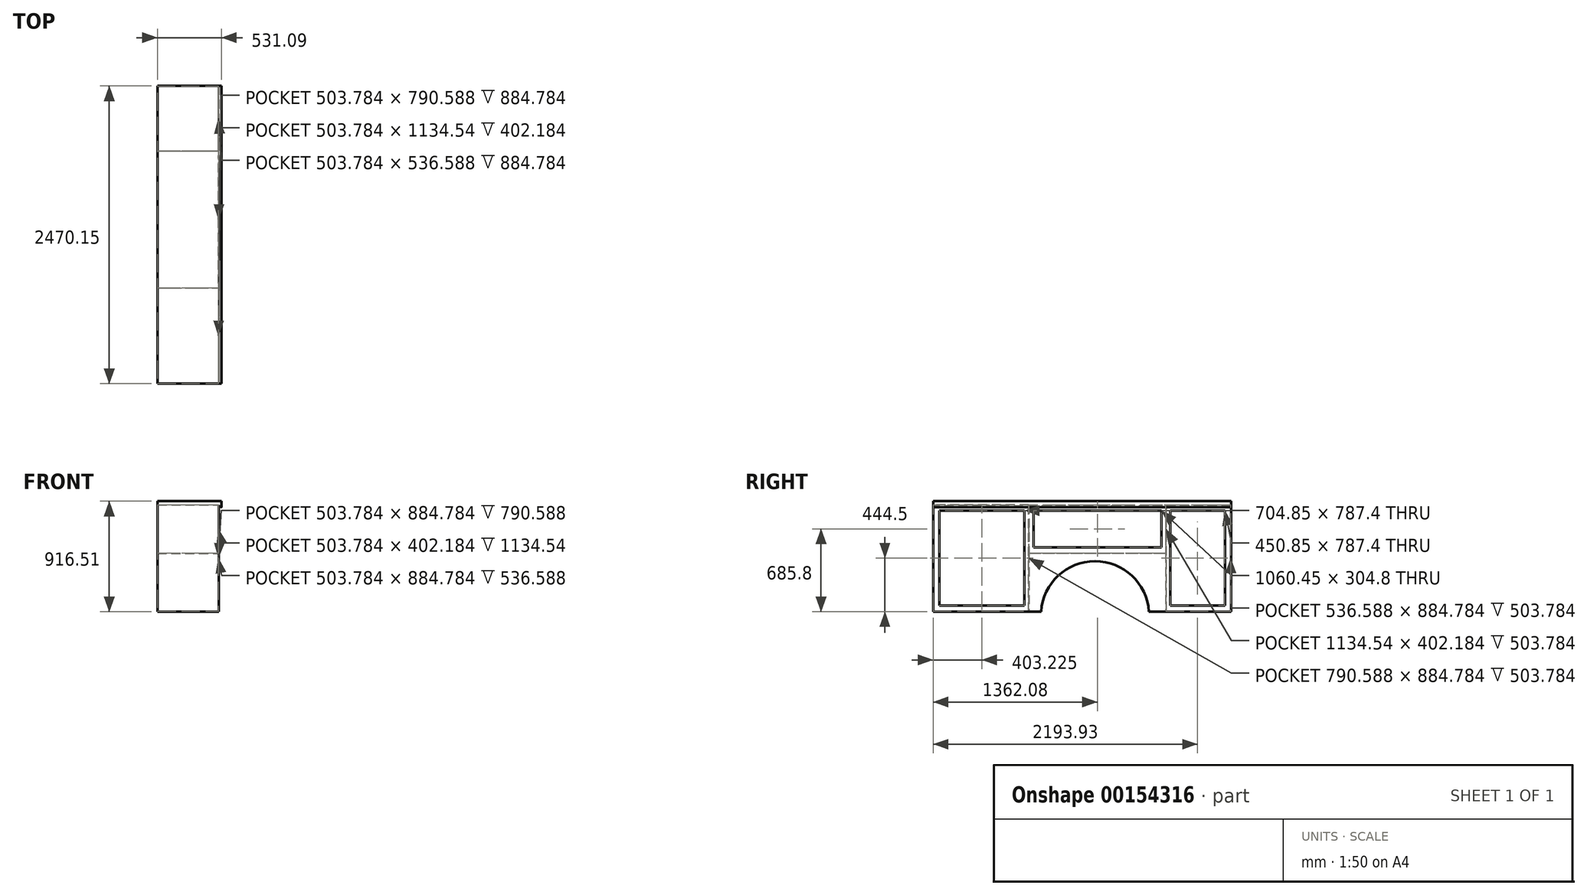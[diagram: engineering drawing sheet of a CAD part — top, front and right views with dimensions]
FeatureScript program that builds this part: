
annotation { "Feature Type Name" : "Feature", "Feature Type Description" : "" }
export const myFeature = defineFeature(function(context is Context, id is Id, definition is map)
    precondition{}
    {
        {
            var Q0;
            Q0=qCreatedBy(makeId("Front.planeOp"),FACE);
            var sketch = newSketch(context, id + "F0", { "sketchPlane" : qUnion([Q0])});
            skLineSegment(sketch, "E0.bottom", {"start": v(-254, 457.2) * mm, "end": v(254, 457.2) * mm});
            skLineSegment(sketch, "E0.top", {"start": v(-254, -457.2) * mm, "end": v(254, -457.2) * mm});
            skLineSegment(sketch, "E0.left", {"start": v(-254, 457.2) * mm, "end": v(-254, -457.2) * mm});
            skLineSegment(sketch, "E0.right", {"start": v(254, 457.2) * mm, "end": v(254, -457.2) * mm});
            skPoint(sketch, "E0.middle", {"position": v(0, 0) * mm});
            skSolve(sketch);
        }
        {
            var Q0;
            Q0 = qSketchRegion(id + "F0", true);
            extrude(context, id + "F1", {"entities" : qUnion([Q0]), "oppositeDirection" : true, "depth" : 2470.15 * mm});
        }
        {
            var Q0;
            Q0=makeQuery(id+"F1.opExtrude","SWEPT_FACE",FACE,{"disambiguationData":[OSD([sQuery(id+"F0.wireOp",EDGE,"E0.right")])]});
            var sketch = newSketch(context, id + "F2", { "sketchPlane" : qUnion([Q0])});
            skLineSegment(sketch, "E1", {"start": v(793.75, 457.2) * mm, "end": v(793.75, -457.2) * mm});
            skLineSegment(sketch, "E2", {"start": v(1930.4, 457.2) * mm, "end": v(1930.4, -457.2) * mm});
            skLineSegment(sketch, "E3", {"start": v(793.75, 25.4) * mm, "end": v(1930.4, 25.4) * mm});
            skLineSegment(sketch, "E4.bottom", {"start": v(755.65, -406.4) * mm, "end": v(50.8, -406.4) * mm});
            skLineSegment(sketch, "E4.top", {"start": v(755.65, 381) * mm, "end": v(50.8, 381) * mm});
            skLineSegment(sketch, "E4.left", {"start": v(755.65, -406.4) * mm, "end": v(755.65, 381) * mm});
            skLineSegment(sketch, "E4.right", {"start": v(50.8, -406.4) * mm, "end": v(50.8, 381) * mm});
            skLineSegment(sketch, "E5.bottom", {"start": v(831.85, 381) * mm, "end": v(1892.3, 381) * mm});
            skLineSegment(sketch, "E5.top", {"start": v(831.85, 76.2) * mm, "end": v(1892.3, 76.2) * mm});
            skLineSegment(sketch, "E5.left", {"start": v(831.85, 381) * mm, "end": v(831.85, 76.2) * mm});
            skLineSegment(sketch, "E5.right", {"start": v(1892.3, 381) * mm, "end": v(1892.3, 76.2) * mm});
            skLineSegment(sketch, "E6.bottom", {"start": v(1968.5, 381) * mm, "end": v(2419.35, 381) * mm});
            skLineSegment(sketch, "E6.top", {"start": v(1968.5, -406.4) * mm, "end": v(2419.35, -406.4) * mm});
            skLineSegment(sketch, "E6.left", {"start": v(1968.5, 381) * mm, "end": v(1968.5, -406.4) * mm});
            skLineSegment(sketch, "E6.right", {"start": v(2419.35, 381) * mm, "end": v(2419.35, -406.4) * mm});
            skSolve(sketch);
        }
        {
            var Q0;
            Q0 = qSketchRegion(id + "F2", true);
            extrude(context, id + "F3", {"entities" : qUnion([Q0]), "operationType" : NewBodyOperationType.REMOVE, "oppositeDirection" : true, "depth" : 505.9 * mm});
        }
        {
            var Q0;
            Q0=makeQuery(id+"F3.boolean.opBoolean","COPY",FACE,{"derivedFrom":makeQuery(id+"F3.opExtrude","SWEPT_FACE",FACE,{"disambiguationData":[OSD([sQuery(id+"F2.wireOp",EDGE,"E4.bottom")])]})});
            var sketch = newSketch(context, id + "F4", { "sketchPlane" : qUnion([Q0])});
            skLineSegment(sketch, "E7.bottom", {"start": v(-251.9, 755.65) * mm, "end": v(251.9, 755.65) * mm});
            skLineSegment(sketch, "E7.top", {"start": v(-251.9, 50.8) * mm, "end": v(251.9, 50.8) * mm});
            skLineSegment(sketch, "E7.left", {"start": v(-251.9, 755.65) * mm, "end": v(-251.9, 50.8) * mm});
            skLineSegment(sketch, "E7.right", {"start": v(251.9, 755.65) * mm, "end": v(251.9, 50.8) * mm});
            skSolve(sketch);
        }
        {
            var Q0;
            Q0 = qSketchRegion(id + "F4", true);
            extrude(context, id + "F5", {"entities" : qUnion([Q0]), "operationType" : NewBodyOperationType.REMOVE, "oppositeDirection" : true, "depth" : 48.7 * mm});
        }
        {
            var Q0;
            Q0=makeQuery(id+"F3.boolean.opBoolean","COPY",FACE,{"derivedFrom":makeQuery(id+"F3.opExtrude","SWEPT_FACE",FACE,{"disambiguationData":[OSD([sQuery(id+"F2.wireOp",EDGE,"E4.top")])]})});
            var sketch = newSketch(context, id + "F6", { "sketchPlane" : qUnion([Q0])});
            skLineSegment(sketch, "E8.bottom", {"start": v(-251.9, -755.65) * mm, "end": v(251.9, -755.65) * mm});
            skLineSegment(sketch, "E8.top", {"start": v(-251.9, -50.8) * mm, "end": v(251.9, -50.8) * mm});
            skLineSegment(sketch, "E8.left", {"start": v(-251.9, -755.65) * mm, "end": v(-251.9, -50.8) * mm});
            skLineSegment(sketch, "E8.right", {"start": v(251.9, -755.65) * mm, "end": v(251.9, -50.8) * mm});
            skSolve(sketch);
        }
        {
            var Q0;
            Q0 = qSketchRegion(id + "F6", true);
            extrude(context, id + "F7", {"entities" : qUnion([Q0]), "operationType" : NewBodyOperationType.REMOVE, "oppositeDirection" : true, "depth" : 48.7 * mm});
        }
        {
            var Q0;
            Q0=makeQuery(id+"F7.boolean.opBoolean","MERGE",FACE,{"derivedFrom":[makeQuery(id+"F5.boolean.opBoolean","MERGE",FACE,{"derivedFrom":[makeQuery(id+"F3.boolean.opBoolean","COPY",FACE,{"derivedFrom":makeQuery(id+"F3.opExtrude","SWEPT_FACE",FACE,{"disambiguationData":[OSD([sQuery(id+"F2.wireOp",EDGE,"E4.right")])]})}),makeQuery(id+"F5.opExtrude","SWEPT_FACE",FACE,{"disambiguationData":[OSD([sQuery(id+"F4.wireOp",EDGE,"E7.top")])]})]}),makeQuery(id+"F7.opExtrude","SWEPT_FACE",FACE,{"disambiguationData":[OSD([sQuery(id+"F6.wireOp",EDGE,"E8.top")])]})]});
            var sketch = newSketch(context, id + "F8", { "sketchPlane" : qUnion([Q0])});
            skLineSegment(sketch, "E9.bottom", {"start": v(251.9, 429.7) * mm, "end": v(-251.9, 429.7) * mm});
            skLineSegment(sketch, "E9.top", {"start": v(251.9, -455.1) * mm, "end": v(-251.9, -455.1) * mm});
            skLineSegment(sketch, "E9.left", {"start": v(251.9, 429.7) * mm, "end": v(251.9, -455.1) * mm});
            skLineSegment(sketch, "E9.right", {"start": v(-251.9, 429.7) * mm, "end": v(-251.9, -455.1) * mm});
            skSolve(sketch);
        }
        {
            var Q0;
            Q0 = qSketchRegion(id + "F8", true);
            extrude(context, id + "F9", {"entities" : qUnion([Q0]), "operationType" : NewBodyOperationType.REMOVE, "oppositeDirection" : true, "depth" : 48.7 * mm});
        }
        {
            var Q0;
            Q0=makeQuery(id+"F7.boolean.opBoolean","MERGE",FACE,{"derivedFrom":[makeQuery(id+"F5.boolean.opBoolean","MERGE",FACE,{"derivedFrom":[makeQuery(id+"F3.boolean.opBoolean","COPY",FACE,{"derivedFrom":makeQuery(id+"F3.opExtrude","SWEPT_FACE",FACE,{"disambiguationData":[OSD([sQuery(id+"F2.wireOp",EDGE,"E4.left")])]})}),makeQuery(id+"F5.opExtrude","SWEPT_FACE",FACE,{"disambiguationData":[OSD([sQuery(id+"F4.wireOp",EDGE,"E7.bottom")])]})]}),makeQuery(id+"F7.opExtrude","SWEPT_FACE",FACE,{"disambiguationData":[OSD([sQuery(id+"F6.wireOp",EDGE,"E8.bottom")])]})]});
            var sketch = newSketch(context, id + "F10", { "sketchPlane" : qUnion([Q0])});
            skLineSegment(sketch, "E10.bottom", {"start": v(-251.9, -455.1) * mm, "end": v(251.9, -455.1) * mm});
            skLineSegment(sketch, "E10.top", {"start": v(-251.9, 429.7) * mm, "end": v(251.9, 429.7) * mm});
            skLineSegment(sketch, "E10.left", {"start": v(-251.9, -455.1) * mm, "end": v(-251.9, 429.7) * mm});
            skLineSegment(sketch, "E10.right", {"start": v(251.9, -455.1) * mm, "end": v(251.9, 429.7) * mm});
            skSolve(sketch);
        }
        {
            var Q0;
            Q0 = qSketchRegion(id + "F10", true);
            extrude(context, id + "F11", {"entities" : qUnion([Q0]), "operationType" : NewBodyOperationType.REMOVE, "oppositeDirection" : true, "depth" : 37.05 * mm});
        }
        {
            var Q0;
            Q0=makeQuery(id+"F3.boolean.opBoolean","COPY",FACE,{"derivedFrom":makeQuery(id+"F3.opExtrude","SWEPT_FACE",FACE,{"disambiguationData":[OSD([sQuery(id+"F2.wireOp",EDGE,"E5.top")])]})});
            var sketch = newSketch(context, id + "F12", { "sketchPlane" : qUnion([Q0])});
            skLineSegment(sketch, "E11.bottom", {"start": v(-251.9, 831.85) * mm, "end": v(251.9, 831.85) * mm});
            skLineSegment(sketch, "E11.top", {"start": v(-251.9, 1892.3) * mm, "end": v(251.9, 1892.3) * mm});
            skLineSegment(sketch, "E11.left", {"start": v(-251.9, 831.85) * mm, "end": v(-251.9, 1892.3) * mm});
            skLineSegment(sketch, "E11.right", {"start": v(251.9, 831.85) * mm, "end": v(251.9, 1892.3) * mm});
            skSolve(sketch);
        }
        {
            var Q0;
            Q0 = qSketchRegion(id + "F12", true);
            extrude(context, id + "F13", {"entities" : qUnion([Q0]), "operationType" : NewBodyOperationType.REMOVE, "oppositeDirection" : true, "depth" : 48.7 * mm});
        }
        {
            var Q0;
            Q0=makeQuery(id+"F3.boolean.opBoolean","COPY",FACE,{"derivedFrom":makeQuery(id+"F3.opExtrude","SWEPT_FACE",FACE,{"disambiguationData":[OSD([sQuery(id+"F2.wireOp",EDGE,"E5.bottom")])]})});
            var sketch = newSketch(context, id + "F14", { "sketchPlane" : qUnion([Q0])});
            skLineSegment(sketch, "E12.bottom", {"start": v(-251.9, -1892.3) * mm, "end": v(251.9, -1892.3) * mm});
            skLineSegment(sketch, "E12.top", {"start": v(-251.9, -831.85) * mm, "end": v(251.9, -831.85) * mm});
            skLineSegment(sketch, "E12.left", {"start": v(-251.9, -1892.3) * mm, "end": v(-251.9, -831.85) * mm});
            skLineSegment(sketch, "E12.right", {"start": v(251.9, -1892.3) * mm, "end": v(251.9, -831.85) * mm});
            skSolve(sketch);
        }
        {
            var Q0;
            Q0 = qSketchRegion(id + "F14", true);
            extrude(context, id + "F15", {"entities" : qUnion([Q0]), "operationType" : NewBodyOperationType.REMOVE, "oppositeDirection" : true, "depth" : 48.7 * mm});
        }
        {
            var Q0;
            Q0=makeQuery(id+"F15.boolean.opBoolean","MERGE",FACE,{"derivedFrom":[makeQuery(id+"F13.boolean.opBoolean","MERGE",FACE,{"derivedFrom":[makeQuery(id+"F3.boolean.opBoolean","COPY",FACE,{"derivedFrom":makeQuery(id+"F3.opExtrude","SWEPT_FACE",FACE,{"disambiguationData":[OSD([sQuery(id+"F2.wireOp",EDGE,"E5.left")])]})}),makeQuery(id+"F13.opExtrude","SWEPT_FACE",FACE,{"disambiguationData":[OSD([sQuery(id+"F12.wireOp",EDGE,"E11.bottom")])]})]}),makeQuery(id+"F15.opExtrude","SWEPT_FACE",FACE,{"disambiguationData":[OSD([sQuery(id+"F14.wireOp",EDGE,"E12.top")])]})]});
            var sketch = newSketch(context, id + "F16", { "sketchPlane" : qUnion([Q0])});
            skLineSegment(sketch, "E13.bottom", {"start": v(251.9, 429.7) * mm, "end": v(-251.9, 429.7) * mm});
            skLineSegment(sketch, "E13.top", {"start": v(251.9, 27.5) * mm, "end": v(-251.9, 27.5) * mm});
            skLineSegment(sketch, "E13.left", {"start": v(251.9, 429.7) * mm, "end": v(251.9, 27.5) * mm});
            skLineSegment(sketch, "E13.right", {"start": v(-251.9, 429.7) * mm, "end": v(-251.9, 27.5) * mm});
            skSolve(sketch);
        }
        {
            var Q0;
            Q0 = qSketchRegion(id + "F16", true);
            extrude(context, id + "F17", {"entities" : qUnion([Q0]), "operationType" : NewBodyOperationType.REMOVE, "oppositeDirection" : true, "depth" : 37.05 * mm});
        }
        {
            var Q0;
            Q0=makeQuery(id+"F15.boolean.opBoolean","MERGE",FACE,{"derivedFrom":[makeQuery(id+"F13.boolean.opBoolean","MERGE",FACE,{"derivedFrom":[makeQuery(id+"F3.boolean.opBoolean","COPY",FACE,{"derivedFrom":makeQuery(id+"F3.opExtrude","SWEPT_FACE",FACE,{"disambiguationData":[OSD([sQuery(id+"F2.wireOp",EDGE,"E5.right")])]})}),makeQuery(id+"F13.opExtrude","SWEPT_FACE",FACE,{"disambiguationData":[OSD([sQuery(id+"F12.wireOp",EDGE,"E11.top")])]})]}),makeQuery(id+"F15.opExtrude","SWEPT_FACE",FACE,{"disambiguationData":[OSD([sQuery(id+"F14.wireOp",EDGE,"E12.bottom")])]})]});
            var sketch = newSketch(context, id + "F18", { "sketchPlane" : qUnion([Q0])});
            skLineSegment(sketch, "E14.bottom", {"start": v(-251.9, 429.7) * mm, "end": v(251.9, 429.7) * mm});
            skLineSegment(sketch, "E14.top", {"start": v(-251.9, 27.5) * mm, "end": v(251.9, 27.5) * mm});
            skLineSegment(sketch, "E14.left", {"start": v(-251.9, 429.7) * mm, "end": v(-251.9, 27.5) * mm});
            skLineSegment(sketch, "E14.right", {"start": v(251.9, 429.7) * mm, "end": v(251.9, 27.5) * mm});
            skSolve(sketch);
        }
        {
            var Q0;
            Q0 = qSketchRegion(id + "F18", true);
            extrude(context, id + "F19", {"entities" : qUnion([Q0]), "operationType" : NewBodyOperationType.REMOVE, "oppositeDirection" : true, "depth" : 37.05 * mm});
        }
        {
            var Q0;
            Q0=makeQuery(id+"F3.boolean.opBoolean","COPY",FACE,{"derivedFrom":makeQuery(id+"F3.opExtrude","SWEPT_FACE",FACE,{"disambiguationData":[OSD([sQuery(id+"F2.wireOp",EDGE,"E6.top")])]})});
            var sketch = newSketch(context, id + "F20", { "sketchPlane" : qUnion([Q0])});
            skLineSegment(sketch, "E15.bottom", {"start": v(-251.9, 1968.5) * mm, "end": v(251.9, 1968.5) * mm});
            skLineSegment(sketch, "E15.top", {"start": v(-251.9, 2419.35) * mm, "end": v(251.9, 2419.35) * mm});
            skLineSegment(sketch, "E15.left", {"start": v(-251.9, 1968.5) * mm, "end": v(-251.9, 2419.35) * mm});
            skLineSegment(sketch, "E15.right", {"start": v(251.9, 1968.5) * mm, "end": v(251.9, 2419.35) * mm});
            skSolve(sketch);
        }
        {
            var Q0;
            Q0 = qSketchRegion(id + "F20", true);
            extrude(context, id + "F21", {"entities" : qUnion([Q0]), "operationType" : NewBodyOperationType.REMOVE, "oppositeDirection" : true, "depth" : 48.7 * mm});
        }
        {
            var Q0;
            Q0=makeQuery(id+"F3.boolean.opBoolean","COPY",FACE,{"derivedFrom":makeQuery(id+"F3.opExtrude","SWEPT_FACE",FACE,{"disambiguationData":[OSD([sQuery(id+"F2.wireOp",EDGE,"E6.bottom")])]})});
            var sketch = newSketch(context, id + "F22", { "sketchPlane" : qUnion([Q0])});
            skLineSegment(sketch, "E16.bottom", {"start": v(-251.9, -1968.5) * mm, "end": v(251.9, -1968.5) * mm});
            skLineSegment(sketch, "E16.top", {"start": v(-251.9, -2419.35) * mm, "end": v(251.9, -2419.35) * mm});
            skLineSegment(sketch, "E16.left", {"start": v(-251.9, -1968.5) * mm, "end": v(-251.9, -2419.35) * mm});
            skLineSegment(sketch, "E16.right", {"start": v(251.9, -1968.5) * mm, "end": v(251.9, -2419.35) * mm});
            skSolve(sketch);
        }
        {
            var Q0;
            Q0 = qSketchRegion(id + "F22", true);
            extrude(context, id + "F23", {"entities" : qUnion([Q0]), "operationType" : NewBodyOperationType.REMOVE, "oppositeDirection" : true, "depth" : 48.7 * mm});
        }
        {
            var Q0;
            Q0=makeQuery(id+"F23.boolean.opBoolean","MERGE",FACE,{"derivedFrom":[makeQuery(id+"F21.boolean.opBoolean","MERGE",FACE,{"derivedFrom":[makeQuery(id+"F3.boolean.opBoolean","COPY",FACE,{"derivedFrom":makeQuery(id+"F3.opExtrude","SWEPT_FACE",FACE,{"disambiguationData":[OSD([sQuery(id+"F2.wireOp",EDGE,"E6.left")])]})}),makeQuery(id+"F21.opExtrude","SWEPT_FACE",FACE,{"disambiguationData":[OSD([sQuery(id+"F20.wireOp",EDGE,"E15.bottom")])]})]}),makeQuery(id+"F23.opExtrude","SWEPT_FACE",FACE,{"disambiguationData":[OSD([sQuery(id+"F22.wireOp",EDGE,"E16.bottom")])]})]});
            var sketch = newSketch(context, id + "F24", { "sketchPlane" : qUnion([Q0])});
            skLineSegment(sketch, "E17.bottom", {"start": v(251.9, -455.1) * mm, "end": v(-251.9, -455.1) * mm});
            skLineSegment(sketch, "E17.top", {"start": v(251.9, 429.7) * mm, "end": v(-251.9, 429.7) * mm});
            skLineSegment(sketch, "E17.left", {"start": v(251.9, -455.1) * mm, "end": v(251.9, 429.7) * mm});
            skLineSegment(sketch, "E17.right", {"start": v(-251.9, -455.1) * mm, "end": v(-251.9, 429.7) * mm});
            skSolve(sketch);
        }
        {
            var Q0;
            Q0 = qSketchRegion(id + "F24", true);
            extrude(context, id + "F25", {"entities" : qUnion([Q0]), "operationType" : NewBodyOperationType.REMOVE, "oppositeDirection" : true, "depth" : 37.05 * mm});
        }
        {
            var Q0;
            Q0=makeQuery(id+"F23.boolean.opBoolean","MERGE",FACE,{"derivedFrom":[makeQuery(id+"F21.boolean.opBoolean","MERGE",FACE,{"derivedFrom":[makeQuery(id+"F3.boolean.opBoolean","COPY",FACE,{"derivedFrom":makeQuery(id+"F3.opExtrude","SWEPT_FACE",FACE,{"disambiguationData":[OSD([sQuery(id+"F2.wireOp",EDGE,"E6.right")])]})}),makeQuery(id+"F21.opExtrude","SWEPT_FACE",FACE,{"disambiguationData":[OSD([sQuery(id+"F20.wireOp",EDGE,"E15.top")])]})]}),makeQuery(id+"F23.opExtrude","SWEPT_FACE",FACE,{"disambiguationData":[OSD([sQuery(id+"F22.wireOp",EDGE,"E16.top")])]})]});
            var sketch = newSketch(context, id + "F26", { "sketchPlane" : qUnion([Q0])});
            skLineSegment(sketch, "E18.bottom", {"start": v(-251.9, -455.1) * mm, "end": v(251.9, -455.1) * mm});
            skLineSegment(sketch, "E18.top", {"start": v(-251.9, 429.7) * mm, "end": v(251.9, 429.7) * mm});
            skLineSegment(sketch, "E18.left", {"start": v(-251.9, -455.1) * mm, "end": v(-251.9, 429.7) * mm});
            skLineSegment(sketch, "E18.right", {"start": v(251.9, -455.1) * mm, "end": v(251.9, 429.7) * mm});
            skSolve(sketch);
        }
        {
            var Q0;
            Q0 = qSketchRegion(id + "F26", true);
            extrude(context, id + "F27", {"entities" : qUnion([Q0]), "operationType" : NewBodyOperationType.REMOVE, "oppositeDirection" : true, "depth" : 48.7 * mm});
        }
        {
            var Q0;
            Q0=makeQuery(id+"F1.opExtrude","SWEPT_FACE",FACE,{"disambiguationData":[OSD([sQuery(id+"F0.wireOp",EDGE,"E0.top")])]});
            var sketch = newSketch(context, id + "F28", { "sketchPlane" : qUnion([Q0])});
            skLineSegment(sketch, "E19.bottom", {"start": v(-254, -1929.35) * mm, "end": v(251.9, -1929.35) * mm});
            skLineSegment(sketch, "E19.top", {"start": v(-254, -794.8) * mm, "end": v(251.9, -794.8) * mm});
            skLineSegment(sketch, "E19.left", {"start": v(-254, -1929.35) * mm, "end": v(-254, -794.8) * mm});
            skLineSegment(sketch, "E19.right", {"start": v(251.9, -1929.35) * mm, "end": v(251.9, -794.8) * mm});
            skSolve(sketch);
        }
        {
            var Q0;
            Q0 = qSketchRegion(id + "F28", true);
            extrude(context, id + "F29", {"entities" : qUnion([Q0]), "operationType" : NewBodyOperationType.REMOVE, "oppositeDirection" : true, "depth" : 482.6 * mm});
        }
        {
            var Q0;
            Q0=makeQuery(id+"F1.opExtrude","SWEPT_FACE",FACE,{"disambiguationData":[OSD([sQuery(id+"F0.wireOp",EDGE,"E0.right")])]});
            var sketch = newSketch(context, id + "F30", { "sketchPlane" : qUnion([Q0])});
            skArc(sketch, "E20", {"start": v(1789.65, -457.2) * mm, "mid": v(1343.03, -38.1) * mm, "end": v(896.4, -457.2) * mm});
            skPoint(sketch, "E21", {"position": v(1343.03, -38.1) * mm});
            skLineSegment(sketch, "E22", {"start": v(1789.65, -457.2) * mm, "end": v(896.4, -457.2) * mm});
            skSolve(sketch);
        }
        {
            var Q0;
            Q0 = qSketchRegion(id + "F30", true);
            extrude(context, id + "F31", {"entities" : qUnion([Q0]), "operationType" : NewBodyOperationType.REMOVE, "endBound" : BoundingType.THROUGH_ALL, "oppositeDirection" : true, "depth" : 25.4 * mm});
        }
        {
            var Q0;
            Q0=makeQuery(id+"F1.opExtrude","CAP_FACE",FACE,{"disambiguationData":[OSD([sQuery(id+"F0.wireOp",EDGE,"E0.bottom"),sQuery(id+"F0.wireOp",EDGE,"E0.top"),sQuery(id+"F0.wireOp",EDGE,"E0.left"),sQuery(id+"F0.wireOp",EDGE,"E0.right")])],"isStart":true});
            var sketch = newSketch(context, id + "F32", { "sketchPlane" : qUnion([Q0])});
            skLineSegment(sketch, "E23", {"start": v(-254, 459.3) * mm, "end": v(277.09, 459.3) * mm});
            skLineSegment(sketch, "E24", {"start": v(277.09, 459.3) * mm, "end": v(277.09, 408.5) * mm});
            skLineSegment(sketch, "E25", {"start": v(277.09, 408.5) * mm, "end": v(254, 419.1) * mm});
            skLineSegment(sketch, "E26", {"start": v(254, 457.2) * mm, "end": v(-254, 457.2) * mm});
            skLineSegment(sketch, "E27", {"start": v(-254, 457.2) * mm, "end": v(-254, 459.3) * mm});
            skLineSegment(sketch, "E28", {"start": v(254, 419.1) * mm, "end": v(254, 457.2) * mm});
            skSolve(sketch);
        }
        {
            var Q0;
            Q0 = qSketchRegion(id + "F32", true);
            var Q1;
            Q1=makeQuery(id+"F1.opExtrude","CAP_FACE",FACE,{"disambiguationData":[OSD([sQuery(id+"F0.wireOp",EDGE,"E0.bottom"),sQuery(id+"F0.wireOp",EDGE,"E0.top"),sQuery(id+"F0.wireOp",EDGE,"E0.left"),sQuery(id+"F0.wireOp",EDGE,"E0.right")])],"isStart":false});
            extrude(context, id + "F33", {"entities" : qUnion([Q0]), "operationType" : NewBodyOperationType.ADD, "endBound" : BoundingType.UP_TO_SURFACE, "oppositeDirection" : true, "endBoundEntityFace" : qUnion([Q1]), "depth" : 25.4 * mm});
        }
        {
            var Q0;
            Q0=makeQuery(id+"Fb1zswCZUndGC3U_1.boolean.opBoolean","MERGE",EDGE,{"derivedFrom":[makeQuery(id+"F33.opExtrude","SWEPT_EDGE",EDGE,{"disambiguationData":[OSD([sQuery(id+"F32.wireOp",EDGE,"E24"),sQuery(id+"F32.wireOp",EDGE,"E25")])]}),makeQuery(id+"Fb1zswCZUndGC3U_1.opExtrude","SWEPT_EDGE",EDGE,{"disambiguationData":[OSD([sQuery(id+"FRRv98LMV5AXUnK_1.wireOp",EDGE,"D8V1SaBw-2kq6-xMgQ-PR26-S25w2Cafi0jA"),sQuery(id+"FRRv98LMV5AXUnK_1.wireOp",EDGE,"AMXTDFUJ-JTe4-3U6D-qmS2-gQZMpLdKAEUP")])]})]});
            fillet(context, id + "F34", {"entities" : qUnion([Q0]), "radius" : 0.5 * mm, "tangentPropagation" : true, "allowEdgeOverflow" : false});
        }
    });
